# Revit family: MidUnit-Vitra-ValarteSeries-62246+62247+62248+62249+62250+62251
name_source: partatom
category: Furniture Systems
revit_build: Autodesk Revit 2017 (Build: 20160225_1515(x64)
units: mm (PartAtom-declared; Revit-internal decimal feet)

## family parameters
Cut with Voids When Loaded = No
Host = Face
OmniClass Number = 23.40.00.00
OmniClass Title = Equipment and Furnishings
Part Type = Normal
Room Calculation Point = No
Round Connector Dimension = Use Diameter
Shared = Yes

## types (6) — shared parameters
BIMobject category = Storage
Construction Type = Face Mounted
Default Elevation = 660 mm
Depth(mm) = 395 mm  [stored 1.29593 ft]
Description = Valarte Mid Unit 55cm
Design country = Turkey
Height(mm) = 830 mm  [stored 2.7231 ft]
IFC Classification = Furniture
Manufacturer = Vitra
Manufacturer name = Vitra
Masterformat 2014 Code = 12 35 30.23
Masterformat 2014 Description = Bathroom Casework
NBS Referans Code = 35-75-08
NBS Referans Description = Bathroom Cabinets
Nominal height = 0.000
Nominal width = 0.000
OmniClass Code = 23-31 25 13
OmniClass Description = Bathroom Cabinets
Product certification = https://vitraglobal.com
Product data url = https://www.vitra.co.uk
Product family = Valarte
Product group = Bathroom Furniture
Technical description = https://www.vitra.co.uk
UNSPSC Code = 30161801
UNSPSC Description = Bathroom Cabinets
URL = https://vitraglobal.com
Uniclass 1.4 Code = L8241
Uniclass 1.4 Description = Bathroom Cabinets
Uniclass 2.0 Code = PR-35-75-08
Uniclass 2.0 Description = Bathroom Cabinets
Uniclass 2015 Code = Pr_40_30_78_03
Uniclass 2015 Name = Bathroom Cabinets
Uniformat II Code = E2010
Uniformat II Description = Fixed Furnishings
Warranty Period (Year) = 2
Weight Net (kg) = 31,000
Width(mm) = 535 mm  [stored 1.75525 ft]
Youtube = https://www.youtube.com

## per-type parameters (varying)
| type | Article No. (default) | Left | Model | Primary Material | Product SKU | Right |
| MidUnit(Left)-Vitra-ValarteSeries_62246 | 62246 | Yes | 62246 | Vitra-MattWhite | 62246 | No |
| MidUnit(Left)-Vitra-ValarteSeries_62247 | 62247 | Yes | 62247 | Vitra-MattGrey | 62247 | No |
| MidUnit(Left)-Vitra-ValarteSeries_62248 | 62248 | Yes | 62248 | Vitra-MattIvory | 62248 | No |
| MidUnit(Right)-Vitra-ValarteSeries_62249 | 62249 | No | 62249 | Vitra-MattWhite | 62249 | Yes |
| MidUnit(Right)-Vitra-ValarteSeries_62250 | 62250 | No | 62250 | Vitra-MattGrey | 62250 | Yes |
| MidUnit(Right)-Vitra-ValarteSeries_62251 | 62251 | No | 62251 | Vitra-MattIvory | 62251 | Yes |

note: [stored X ft] marks values corroborated as IEEE doubles in the binary element streams (Revit-internal decimal feet)

## geometry (parser evidence)
native form markers: Sweep x6
no freeform markers — native parametric forms only
